# Revit family: pl-rp40_160la17_50Hz
name_source: partatom
category: 機械設備
units: mm (PartAtom-declared; Revit-internal decimal feet)

## family parameters
OmniClass タイトル = Split System Air Conditioning Units
OmniClass 番号 = 23.75.10.24.21.27.27
パーツ タイプ = 標準
ロード時にボイドで切り取り = いいえ
丸型コネクタ寸法 = 直径を使用
作業面ベース = いいえ
共有 = いいえ
常に垂直 = はい
部屋計算ポイント = はい

## types (10) — shared parameters
IfcExportAs = IfcUnitaryEquipmentType
IfcExportType = AIRCONDITIONINGUNIT
OmniClassCode = 23-751024212727
URL = https://www.mitsubishielectric.co.jp
Uniclass2015Code = Pr_70_65_03_84
Uniclass2015Title = Split coil remote air cooled condensing units
Uniclass2015Version = Systems v1.9
Width = 650  [stored 2.13255 ft]
ケーブルサイズ = 2 mm
サービススペース = はい
ドレン管径 = 32 mm
企業コード = 108420
冷媒管径 = 100 mm
冷媒高低圧ガス管径 = 0 mm
分類コード = 50053003123020
加湿給水管径 = 0 mm
吊り位置X = 574  [stored 1.8832 ft]
周波数 = 50 Hz
呼称 = パッケージ形空気調和機_室内機
始動方式 = 直入
形式 = カセット形(2方向吹出形)
推奨ブレーカー容量 = 15 A
本体マテリアル = 鋼、ペイント仕上げ、アイボリー、光沢
材質 = 溶融亜鉛メッキ鋼板
極数 = 3
機外静圧 = 0.0 Pa
法定耐用年数 = 15
消費電力 = 0 kW
消費電力_冷房 = 0 kW
消費電力_加湿器 = 0 kW
消費電力_暖房 = 0 kW
消費電力_電気ヒーター = 0 kW
相 = 1
相_電気ヒーター = 1
積算_科目 = 1 空気調和設備
符号 = PAC_CK2
製品リリース年月 = 2021/5/10
製品出荷対象 = 国内
製造元 = 三菱電機株式会社
設置方法 = カセット形(2方向吹出形)
設計冷房能力 = 0 kW
設計冷房能力_顕熱 = 0 kW
設計暖房能力 = 0 kW
説明 = 空冷ヒートポンプインバータPAC天井カセット形(2方向吹出)
負荷分類 = 3_ファン類
運転質量 = 0.00 kg
電動機出力_送風機 = 0 kW
電圧 = 200 V
電圧_電気ヒーター = 0 V
電源種別 = 一般
zero-valued in all types: S_H, 価格, 有効加湿量

## per-type parameters (varying)
- PL-RP40LA17_50Hz: Depth=770  [stored 2.52625 ft]; Height=357  [stored 1.17126 ft]; MAX風量=600.0 m³/h; MID風量=540.0 m³/h; MIN風量=480.0 m³/h; ドレン管高さ=60  [stored 0.19685 ft]; モデル=PL-RP40LA17; 冷媒ガス管径=13 mm; 冷媒ガス管長さ=78  [stored 0.255906 ft]; 冷媒ガス管高さ=122  [stored 0.400262 ft]; 冷媒液管径=6 mm; 冷媒液管長さ=67  [stored 0.219816 ft]; 冷媒液管高さ=122  [stored 0.400262 ft]; 冷媒管径符号=Ac; 冷房能力=4 kW; 吊り位置Y=824  [stored 2.70341 ft]; 吊り金具_高さ=190; 暖房能力=4 kW; 製品質量=21.00 kg; 質量=25.20 kg; 音響パワーレベル(dB)=52; 音響パワーレベル（中）(dB)=51; 音響パワーレベル（弱）(dB)=50; 音響パワーレベル（静）(dB)=49; 風量=600.0 m³/h; 風量（m3／min）=10; 風量（中）（m3／min）=9; 風量（弱）（m3／min）=8; 風量（静）=420; 風量（静）（m3／min）=7
- PL-RP45LA17_50Hz: Depth=940  [stored 3.08399 ft]; Height=357  [stored 1.17126 ft]; MAX風量=690.0 m³/h; MID風量=630.0 m³/h; MIN風量=570.0 m³/h; ドレン管高さ=60  [stored 0.19685 ft]; モデル=PL-RP45LA17; 冷媒ガス管径=13 mm; 冷媒ガス管長さ=78  [stored 0.255906 ft]; 冷媒ガス管高さ=122  [stored 0.400262 ft]; 冷媒液管径=6 mm; 冷媒液管長さ=67  [stored 0.219816 ft]; 冷媒液管高さ=122  [stored 0.400262 ft]; 冷媒管径符号=Ac; 冷房能力=4 kW; 吊り位置Y=994; 吊り金具_高さ=190; 暖房能力=5 kW; 製品質量=24.00 kg; 質量=28.80 kg; 音響パワーレベル(dB)=53; 音響パワーレベル（中）(dB)=52; 音響パワーレベル（弱）(dB)=50; 音響パワーレベル（静）(dB)=49; 風量=690.0 m³/h; 風量（m3／min）=11.5; 風量（中）（m3／min）=10.5; 風量（弱）（m3／min）=9.5; 風量（静）=510; 風量（静）（m3／min）=8.5
- PL-RP50LA17_50Hz: Depth=940  [stored 3.08399 ft]; Height=357  [stored 1.17126 ft]; MAX風量=840.0 m³/h; MID風量=780.0 m³/h; MIN風量=720.0 m³/h; ドレン管高さ=60  [stored 0.19685 ft]; モデル=PL-RP50LA17; 冷媒ガス管径=13 mm; 冷媒ガス管長さ=78  [stored 0.255906 ft]; 冷媒ガス管高さ=122  [stored 0.400262 ft]; 冷媒液管径=6 mm; 冷媒液管長さ=67  [stored 0.219816 ft]; 冷媒液管高さ=122  [stored 0.400262 ft]; 冷媒管径符号=Ac; 冷房能力=5 kW; 吊り位置Y=994; 吊り金具_高さ=190; 暖房能力=5 kW; 製品質量=26.00 kg; 質量=31.20 kg; 音響パワーレベル(dB)=58; 音響パワーレベル（中）(dB)=56; 音響パワーレベル（弱）(dB)=54; 音響パワーレベル（静）(dB)=51; 風量=840.0 m³/h; 風量（m3／min）=14; 風量（中）（m3／min）=13; 風量（弱）（m3／min）=12; 風量（静）=600; 風量（静）（m3／min）=10
- PL-RP56LA17_50Hz: Depth=940  [stored 3.08399 ft]; Height=357  [stored 1.17126 ft]; MAX風量=840.0 m³/h; MID風量=780.0 m³/h; MIN風量=720.0 m³/h; ドレン管高さ=60  [stored 0.19685 ft]; モデル=PL-RP56LA17; 冷媒ガス管径=13 mm; 冷媒ガス管長さ=78  [stored 0.255906 ft]; 冷媒ガス管高さ=122  [stored 0.400262 ft]; 冷媒液管径=6 mm; 冷媒液管長さ=67  [stored 0.219816 ft]; 冷媒液管高さ=122  [stored 0.400262 ft]; 冷媒管径符号=Ac; 冷房能力=5 kW; 吊り位置Y=994; 吊り金具_高さ=190; 暖房能力=6 kW; 製品質量=26.00 kg; 質量=31.20 kg; 音響パワーレベル(dB)=58; 音響パワーレベル（中）(dB)=56; 音響パワーレベル（弱）(dB)=54; 音響パワーレベル（静）(dB)=52; 風量=840.0 m³/h; 風量（m3／min）=14; 風量（中）（m3／min）=13; 風量（弱）（m3／min）=12; 風量（静）=600; 風量（静）（m3／min）=10
- PL-RP63LA17_50Hz: Depth=940  [stored 3.08399 ft]; Height=357  [stored 1.17126 ft]; MAX風量=840.0 m³/h; MID風量=780.0 m³/h; MIN風量=720.0 m³/h; ドレン管高さ=60  [stored 0.19685 ft]; モデル=PL-RP63LA17; 冷媒ガス管径=13 mm; 冷媒ガス管長さ=78  [stored 0.255906 ft]; 冷媒ガス管高さ=122  [stored 0.400262 ft]; 冷媒液管径=6 mm; 冷媒液管長さ=67  [stored 0.219816 ft]; 冷媒液管高さ=122  [stored 0.400262 ft]; 冷媒管径符号=Ac; 冷房能力=6 kW; 吊り位置Y=994; 吊り金具_高さ=190; 暖房能力=6 kW; 製品質量=26.00 kg; 質量=31.20 kg; 音響パワーレベル(dB)=58; 音響パワーレベル（中）(dB)=56; 音響パワーレベル（弱）(dB)=54; 音響パワーレベル（静）(dB)=53; 風量=840.0 m³/h; 風量（m3／min）=14; 風量（中）（m3／min）=13; 風量（弱）（m3／min）=12; 風量（静）=600; 風量（静）（m3／min）=10
- PL-RP71LA17_50Hz: Depth=940  [stored 3.08399 ft]; Height=357  [stored 1.17126 ft]; MAX風量=840.0 m³/h; MID風量=780.0 m³/h; MIN風量=720.0 m³/h; ドレン管高さ=60  [stored 0.19685 ft]; モデル=PL-RP71LA17; 冷媒ガス管径=16 mm; 冷媒ガス管長さ=78  [stored 0.255906 ft]; 冷媒ガス管高さ=122  [stored 0.400262 ft]; 冷媒液管径=10 mm; 冷媒液管長さ=67  [stored 0.219816 ft]; 冷媒液管高さ=122  [stored 0.400262 ft]; 冷媒管径符号=Bd; 冷房能力=6 kW; 吊り位置Y=994; 吊り金具_高さ=190; 暖房能力=7 kW; 製品質量=26.00 kg; 質量=31.20 kg; 音響パワーレベル(dB)=58; 音響パワーレベル（中）(dB)=56; 音響パワーレベル（弱）(dB)=55; 音響パワーレベル（静）(dB)=54; 風量=840.0 m³/h; 風量（m3／min）=14; 風量（中）（m3／min）=13; 風量（弱）（m3／min）=12; 風量（静）=600; 風量（静）（m3／min）=10
- PL-RP80LA17_50Hz: Depth=940  [stored 3.08399 ft]; Height=357  [stored 1.17126 ft]; MAX風量=840.0 m³/h; MID風量=780.0 m³/h; MIN風量=720.0 m³/h; ドレン管高さ=60  [stored 0.19685 ft]; モデル=PL-RP80LA17; 冷媒ガス管径=16 mm; 冷媒ガス管長さ=78  [stored 0.255906 ft]; 冷媒ガス管高さ=122  [stored 0.400262 ft]; 冷媒液管径=10 mm; 冷媒液管長さ=67  [stored 0.219816 ft]; 冷媒液管高さ=122  [stored 0.400262 ft]; 冷媒管径符号=Bg; 冷房能力=7 kW; 吊り位置Y=994; 吊り金具_高さ=190; 暖房能力=8 kW; 製品質量=26.00 kg; 質量=31.20 kg; 音響パワーレベル(dB)=59; 音響パワーレベル（中）(dB)=57; 音響パワーレベル（弱）(dB)=56; 音響パワーレベル（静）(dB)=55; 風量=840.0 m³/h; 風量（m3／min）=14; 風量（中）（m3／min）=13; 風量（弱）（m3／min）=12; 風量（静）=600; 風量（静）（m3／min）=10
- PL-RP112LA17_50Hz: Depth=1440  [stored 4.72441 ft]; Height=398  [stored 1.30577 ft]; MAX風量=1440.0 m³/h; MID風量=1350.0 m³/h; MIN風量=1230.0 m³/h; ドレン管高さ=101  [stored 0.331365 ft]; モデル=PL-RP112LA17; 冷媒ガス管径=16 mm; 冷媒ガス管長さ=83  [stored 0.27231 ft]; 冷媒ガス管高さ=163  [stored 0.534777 ft]; 冷媒液管径=10 mm; 冷媒液管長さ=71  [stored 0.23294 ft]; 冷媒液管高さ=163  [stored 0.534777 ft]; 冷媒管径符号=Bg; 冷房能力=10 kW; 吊り位置Y=1494  [stored 4.90157 ft]; 吊り金具_高さ=231  [stored 0.757874 ft]; 暖房能力=11 kW; 製品質量=45.00 kg; 質量=54.00 kg; 音響パワーレベル(dB)=62; 音響パワーレベル（中）(dB)=61; 音響パワーレベル（弱）(dB)=60; 音響パワーレベル（静）(dB)=58; 風量=1440.0 m³/h; 風量（m3／min）=24; 風量（中）（m3／min）=22.5; 風量（弱）（m3／min）=20.5; 風量（静）=1080; 風量（静）（m3／min）=18
- PL-RP140LA17_50Hz: Depth=1440  [stored 4.72441 ft]; Height=398  [stored 1.30577 ft]; MAX風量=1740.0 m³/h; MID風量=1620.0 m³/h; MIN風量=1470.0 m³/h; ドレン管高さ=101  [stored 0.331365 ft]; モデル=PL-RP140LA17; 冷媒ガス管径=16 mm; 冷媒ガス管長さ=83  [stored 0.27231 ft]; 冷媒ガス管高さ=163  [stored 0.534777 ft]; 冷媒液管径=10 mm; 冷媒液管長さ=71  [stored 0.23294 ft]; 冷媒液管高さ=163  [stored 0.534777 ft]; 冷媒管径符号=Bg; 冷房能力=13 kW; 吊り位置Y=1494  [stored 4.90157 ft]; 吊り金具_高さ=231  [stored 0.757874 ft]; 暖房能力=14 kW; 製品質量=47.00 kg; 質量=56.40 kg; 音響パワーレベル(dB)=66; 音響パワーレベル（中）(dB)=65; 音響パワーレベル（弱）(dB)=62; 音響パワーレベル（静）(dB)=61; 風量=1740.0 m³/h; 風量（m3／min）=29; 風量（中）（m3／min）=27; 風量（弱）（m3／min）=24.5; 風量（静）=1200; 風量（静）（m3／min）=20
- PL-RP160LA17_50Hz: Depth=1440  [stored 4.72441 ft]; Height=398  [stored 1.30577 ft]; MAX風量=1800.0 m³/h; MID風量=1620.0 m³/h; MIN風量=1470.0 m³/h; ドレン管高さ=101  [stored 0.331365 ft]; モデル=PL-RP160LA17; 冷媒ガス管径=16 mm; 冷媒ガス管長さ=83  [stored 0.27231 ft]; 冷媒ガス管高さ=163  [stored 0.534777 ft]; 冷媒液管径=10 mm; 冷媒液管長さ=71  [stored 0.23294 ft]; 冷媒液管高さ=163  [stored 0.534777 ft]; 冷媒管径符号=Bg; 冷房能力=14 kW; 吊り位置Y=1494  [stored 4.90157 ft]; 吊り金具_高さ=231  [stored 0.757874 ft]; 暖房能力=16 kW; 製品質量=47.00 kg; 質量=56.40 kg; 音響パワーレベル(dB)=67; 音響パワーレベル（中）(dB)=66; 音響パワーレベル（弱）(dB)=63; 音響パワーレベル（静）(dB)=62; 風量=1800.0 m³/h; 風量（m3／min）=30; 風量（中）（m3／min）=27; 風量（弱）（m3／min）=24.5; 風量（静）=1200; 風量（静）（m3／min）=20

note: [stored X ft] marks values corroborated as IEEE doubles in the binary element streams (Revit-internal decimal feet)

## geometry (parser evidence)
native form markers: Blend x24
no freeform markers — native parametric forms only
